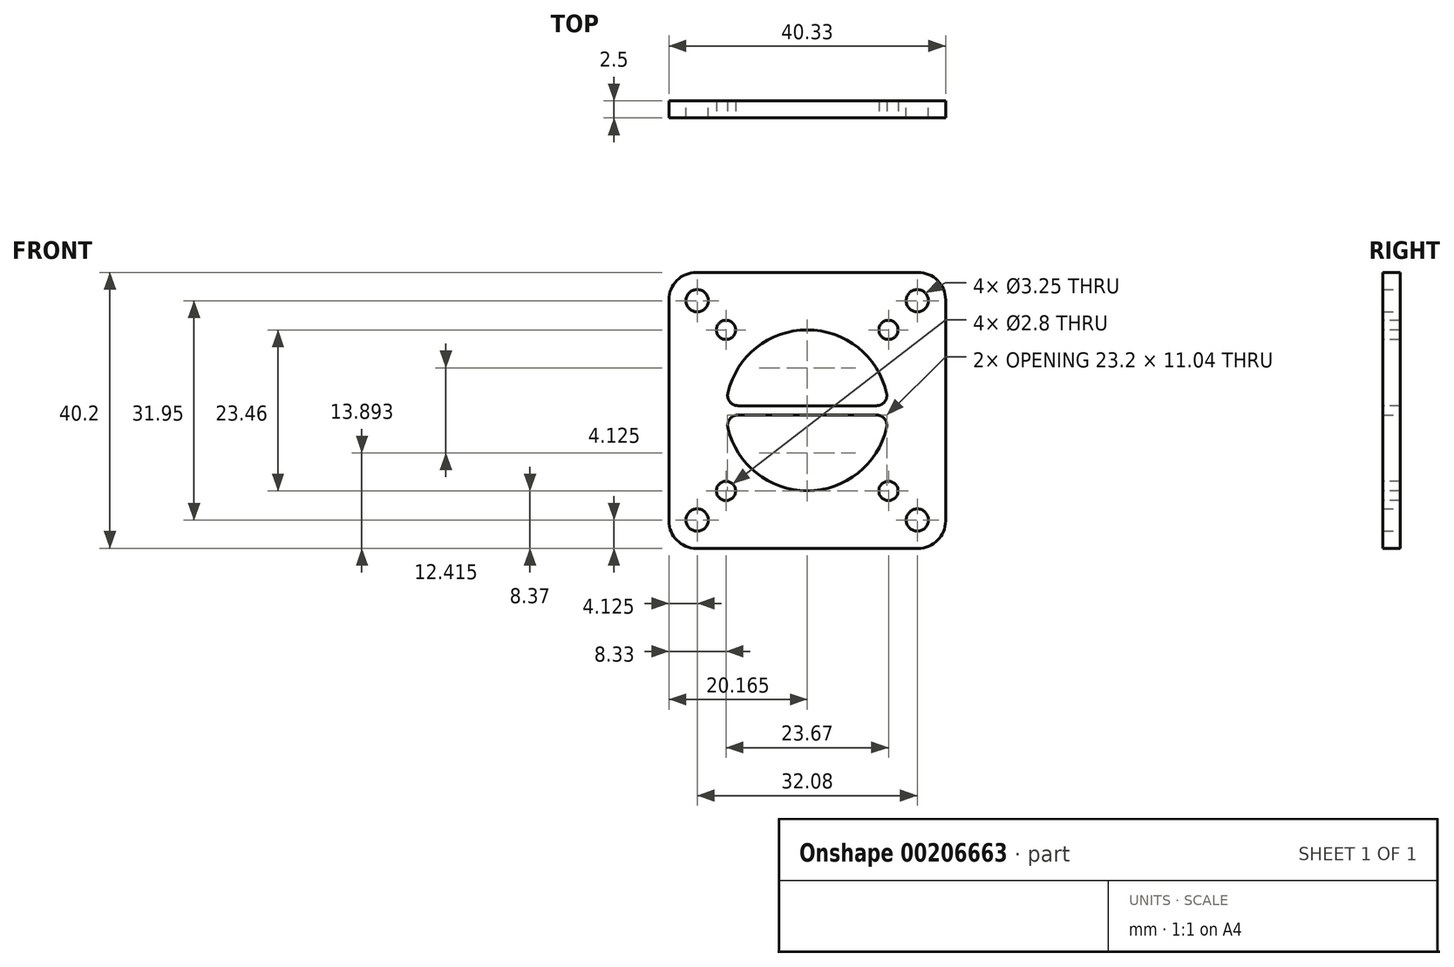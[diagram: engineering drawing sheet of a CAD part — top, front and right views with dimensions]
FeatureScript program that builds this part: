
annotation { "Feature Type Name" : "Feature", "Feature Type Description" : "" }
export const myFeature = defineFeature(function(context is Context, id is Id, definition is map)
    precondition{}
    {
        {
            var Q0;
            Q0=qCreatedBy(makeId("Front.planeOp"),FACE);
            var sketch = newSketch(context, id + "F0", { "sketchPlane" : qUnion([Q0])});
            skLineSegment(sketch, "E0.bottom", {"start": v(4, 0) * mm, "end": v(36.33, 0) * mm});
            skLineSegment(sketch, "E0.top", {"start": v(4, 40.2) * mm, "end": v(36.33, 40.2) * mm});
            skLineSegment(sketch, "E0.left", {"start": v(0, 4) * mm, "end": v(0, 36.2) * mm});
            skLineSegment(sketch, "E0.right", {"start": v(40.33, 4) * mm, "end": v(40.33, 36.2) * mm});
            skCircle(sketch, "E1", {"center": v(4.12, 36.08) * mm, "radius": 1.63 * mm});
            skCircle(sketch, "E2.0.1.0", {"center": v(4.12, 4.13) * mm, "radius": 1.63 * mm});
            skCircle(sketch, "E2.1.0.0", {"center": v(36.2, 36.08) * mm, "radius": 1.63 * mm});
            skCircle(sketch, "E2.1.1.0", {"center": v(36.2, 4.13) * mm, "radius": 1.63 * mm});
            skLineSegment(sketch, "E2.direction1", {"start": v(4.12, 36.08) * mm, "end": v(36.2, 36.08) * mm, "construction": true});
            skLineSegment(sketch, "E2.direction2", {"start": v(4.12, 36.08) * mm, "end": v(4.12, 4.13) * mm, "construction": true});
            skPoint(sketch, "E3.visualSharp", {"position": v(0, 40.2) * mm});
            skArc(sketch, "E3.filletArc", {"start": v(4, 40.2) * mm, "mid": v(1.17, 39.03) * mm, "end": v(0, 36.2) * mm});
            skPoint(sketch, "E4.visualSharp", {"position": v(40.33, 40.2) * mm});
            skArc(sketch, "E4.filletArc", {"start": v(40.33, 36.2) * mm, "mid": v(39.16, 39.03) * mm, "end": v(36.33, 40.2) * mm});
            skPoint(sketch, "E5.visualSharp", {"position": v(40.33, 0) * mm});
            skArc(sketch, "E5.filletArc", {"start": v(36.33, 0) * mm, "mid": v(39.16, 1.17) * mm, "end": v(40.33, 4) * mm});
            skPoint(sketch, "E6.visualSharp", {"position": v(0, 0) * mm});
            skArc(sketch, "E6.filletArc", {"start": v(0, 4) * mm, "mid": v(1.17, 1.17) * mm, "end": v(4, 0) * mm});
            skSolve(sketch);
        }
        {
            var Q0;
            Q0=makeQuery(id+"F0.imprint","IMPRINT",FACE,{"disambiguationData":[TD([[makeQuery(id+"F0.imprint","IMPRINT",EDGE,{"derivedFrom":sQuery(id+"F0.wireOp",EDGE,"E0.bottom")}),1.0]])]});
            extrude(context, id + "F1", {"entities" : qUnion([Q0]), "depth" : 2.5 * mm});
        }
        {
            var Q0;
            Q0=makeQuery(id+"F1.opExtrude","CAP_FACE",FACE,{"disambiguationData":[OSD([sQuery(id+"F0.wireOp",EDGE,"E0.bottom"),sQuery(id+"F0.wireOp",EDGE,"E0.top"),sQuery(id+"F0.wireOp",EDGE,"E0.left"),sQuery(id+"F0.wireOp",EDGE,"E0.right"),sQuery(id+"F0.wireOp",EDGE,"E1"),sQuery(id+"F0.wireOp",EDGE,"E2.0.1.0"),sQuery(id+"F0.wireOp",EDGE,"E2.1.0.0"),sQuery(id+"F0.wireOp",EDGE,"E2.1.1.0"),sQuery(id+"F0.wireOp",EDGE,"E3.filletArc"),sQuery(id+"F0.wireOp",EDGE,"E4.filletArc"),sQuery(id+"F0.wireOp",EDGE,"E5.filletArc"),sQuery(id+"F0.wireOp",EDGE,"E6.filletArc")])],"isStart":false});
            var sketch = newSketch(context, id + "F2", { "sketchPlane" : qUnion([Q0])});
            skLineSegment(sketch, "E7.bottom", {"start": v(35.09, 35.02) * mm, "end": v(5.24, 35.02) * mm});
            skLineSegment(sketch, "E7.top", {"start": v(35.09, 5.19) * mm, "end": v(5.24, 5.18) * mm});
            skLineSegment(sketch, "E7.left", {"start": v(35.09, 35.02) * mm, "end": v(35.09, 5.19) * mm});
            skLineSegment(sketch, "E7.right", {"start": v(5.24, 35.02) * mm, "end": v(5.24, 5.19) * mm});
            skPoint(sketch, "E7.middle", {"position": v(20.16, 20.1) * mm});
            skPoint(sketch, "E7.middle.positionSnap0", {"position": v(40.33, 20.1) * mm});
            skPoint(sketch, "E7.middle.positionSnap1", {"position": v(20.16, 40.2) * mm});
            skPoint(sketch, "E7.centerSnap0", {"position": v(40.33, 20.1) * mm});
            skPoint(sketch, "E7.centerSnap1", {"position": v(20.16, 40.2) * mm});
            skCircle(sketch, "E8", {"center": v(8.33, 31.83) * mm, "radius": 1.4 * mm});
            skCircle(sketch, "E9", {"center": v(32, 31.83) * mm, "radius": 1.4 * mm});
            skCircle(sketch, "E10", {"center": v(32, 8.37) * mm, "radius": 1.4 * mm});
            skCircle(sketch, "E11", {"center": v(8.33, 8.37) * mm, "radius": 1.4 * mm});
            skLineSegment(sketch, "E12.bottom", {"start": v(32, 31.83) * mm, "end": v(8.33, 31.83) * mm, "construction": true});
            skLineSegment(sketch, "E12.top", {"start": v(32, 8.37) * mm, "end": v(8.33, 8.37) * mm, "construction": true});
            skLineSegment(sketch, "E12.left", {"start": v(32, 31.83) * mm, "end": v(32, 8.37) * mm, "construction": true});
            skLineSegment(sketch, "E12.right", {"start": v(8.33, 31.83) * mm, "end": v(8.33, 8.37) * mm, "construction": true});
            skLineSegment(sketch, "E13.bottom", {"start": v(32, 20.79) * mm, "end": v(8.33, 20.79) * mm});
            skLineSegment(sketch, "E13.top", {"start": v(32, 19.42) * mm, "end": v(8.33, 19.42) * mm});
            skLineSegment(sketch, "E13.left", {"start": v(32, 20.79) * mm, "end": v(32, 19.42) * mm});
            skLineSegment(sketch, "E13.right", {"start": v(8.33, 20.79) * mm, "end": v(8.33, 19.42) * mm});
            skArc(sketch, "E14", {"start": v(32, 20.79) * mm, "mid": v(20.16, 31.83) * mm, "end": v(8.33, 20.79) * mm});
            skArc(sketch, "E15", {"start": v(8.33, 19.42) * mm, "mid": v(20.16, 8.37) * mm, "end": v(32, 19.42) * mm});
            skSolve(sketch);
        }
        {
            var Q0;
            Q0=makeQuery(id+"F2.imprint","IMPRINT",FACE,{"disambiguationData":[TD([[makeQuery(id+"F2.imprint","IMPRINT",EDGE,{"derivedFrom":sQuery(id+"F2.wireOp",EDGE,"E8")}),1.0]])]});
            var Q1;
            Q1=makeQuery(id+"F2.imprint","IMPRINT",FACE,{"disambiguationData":[TD([[makeQuery(id+"F2.imprint","IMPRINT",EDGE,{"derivedFrom":sQuery(id+"F2.wireOp",EDGE,"E9")}),1.0]])]});
            var Q2;
            Q2=makeQuery(id+"F2.imprint","IMPRINT",FACE,{"disambiguationData":[TD([[makeQuery(id+"F2.imprint","IMPRINT",EDGE,{"derivedFrom":sQuery(id+"F2.wireOp",EDGE,"E10")}),1.0]])]});
            var Q3;
            Q3=makeQuery(id+"F2.imprint","IMPRINT",FACE,{"disambiguationData":[TD([[makeQuery(id+"F2.imprint","IMPRINT",EDGE,{"derivedFrom":sQuery(id+"F2.wireOp",EDGE,"E11")}),1.0]])]});
            var Q4;
            Q4=makeQuery(id+"F2.imprint","IMPRINT",FACE,{"disambiguationData":[TD([[makeQuery(id+"F2.imprint","IMPRINT",EDGE,{"derivedFrom":sQuery(id+"F2.wireOp",EDGE,"E13.top")}),1.0]])]});
            var Q5;
            Q5=makeQuery(id+"F2.imprint","IMPRINT",FACE,{"disambiguationData":[TD([[makeQuery(id+"F2.imprint","IMPRINT",EDGE,{"derivedFrom":sQuery(id+"F2.wireOp",EDGE,"E13.bottom")}),-1.0]])]});
            extrude(context, id + "F3", {"entities" : qUnion([Q0, Q1, Q2, Q3, Q4, Q5]), "operationType" : NewBodyOperationType.REMOVE, "endBound" : BoundingType.THROUGH_ALL, "oppositeDirection" : true, "depth" : 25 * mm});
        }
        {
            var Q0;
            Q0=makeQuery(id+"F3.boolean.opBoolean","COPY",EDGE,{"derivedFrom":makeQuery(id+"F3.opExtrude","SWEPT_EDGE",EDGE,{"disambiguationData":[OSD([sQuery(id+"F2.wireOp",EDGE,"E13.bottom"),sQuery(id+"F2.wireOp",EDGE,"E13.right"),sQuery(id+"F2.wireOp",EDGE,"E14")])]})});
            var Q1;
            Q1=makeQuery(id+"F3.boolean.opBoolean","COPY",EDGE,{"derivedFrom":makeQuery(id+"F3.opExtrude","SWEPT_EDGE",EDGE,{"disambiguationData":[OSD([sQuery(id+"F2.wireOp",EDGE,"E13.bottom"),sQuery(id+"F2.wireOp",EDGE,"E13.left"),sQuery(id+"F2.wireOp",EDGE,"E14")])]})});
            var Q2;
            Q2=makeQuery(id+"F3.boolean.opBoolean","COPY",EDGE,{"derivedFrom":makeQuery(id+"F3.opExtrude","SWEPT_EDGE",EDGE,{"disambiguationData":[OSD([sQuery(id+"F2.wireOp",EDGE,"E13.top"),sQuery(id+"F2.wireOp",EDGE,"E13.left"),sQuery(id+"F2.wireOp",EDGE,"E15")])]})});
            var Q3;
            Q3=makeQuery(id+"F3.boolean.opBoolean","COPY",EDGE,{"derivedFrom":makeQuery(id+"F3.opExtrude","SWEPT_EDGE",EDGE,{"disambiguationData":[OSD([sQuery(id+"F2.wireOp",EDGE,"E13.top"),sQuery(id+"F2.wireOp",EDGE,"E13.right"),sQuery(id+"F2.wireOp",EDGE,"E15")])]})});
            fillet(context, id + "F4", {"entities" : qUnion([Q0, Q1, Q2, Q3]), "radius" : 1.5 * mm, "tangentPropagation" : true, "allowEdgeOverflow" : false});
        }
    });
